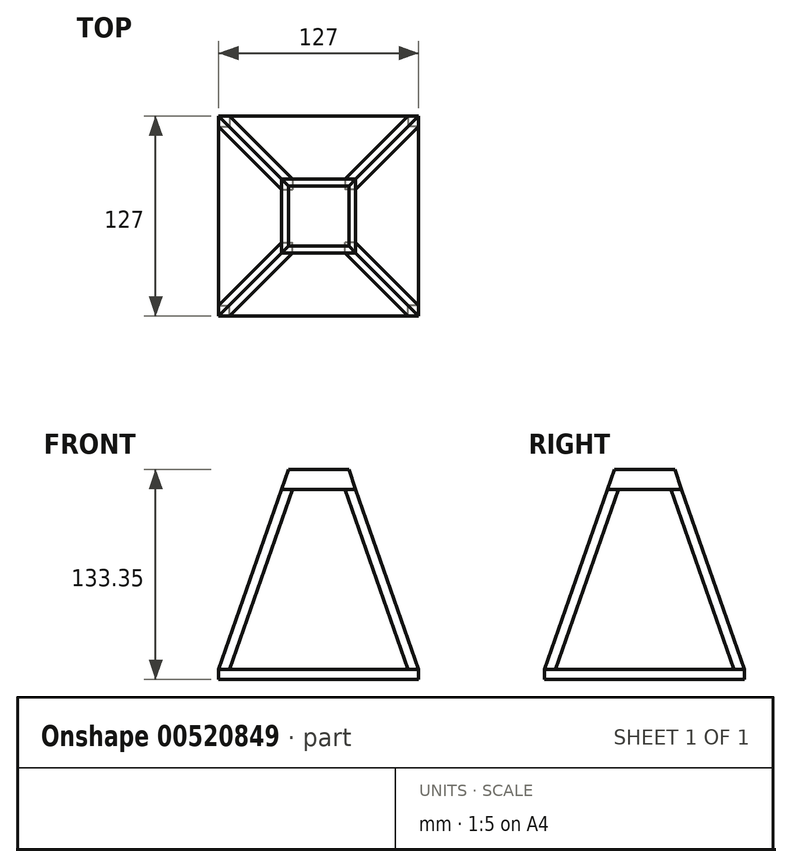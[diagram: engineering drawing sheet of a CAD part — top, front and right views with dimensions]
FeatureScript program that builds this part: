
annotation { "Feature Type Name" : "Feature", "Feature Type Description" : "" }
export const myFeature = defineFeature(function(context is Context, id is Id, definition is map)
    precondition{}
    {
        {
            var Q0;
            Q0=qCreatedBy(makeId("Top.planeOp"),FACE);
            var sketch = newSketch(context, id + "F0", { "sketchPlane" : qUnion([Q0])});
            skLineSegment(sketch, "E0.bottom", {"start": v(-63.5, 63.5) * mm, "end": v(63.5, 63.5) * mm});
            skLineSegment(sketch, "E0.top", {"start": v(-63.5, -63.5) * mm, "end": v(63.5, -63.5) * mm});
            skLineSegment(sketch, "E0.left", {"start": v(-63.5, 63.5) * mm, "end": v(-63.5, -63.5) * mm});
            skLineSegment(sketch, "E0.right", {"start": v(63.5, 63.5) * mm, "end": v(63.5, -63.5) * mm});
            skLineSegment(sketch, "E1", {"start": v(-63.5, 63.5) * mm, "end": v(63.5, -63.5) * mm, "construction": true});
            skLineSegment(sketch, "E2", {"start": v(-63.5, -63.5) * mm, "end": v(63.5, 63.5) * mm, "construction": true});
            skSolve(sketch);
        }
        {
            var Q0;
            Q0 = qSketchRegion(id + "F0", true);
            extrude(context, id + "F1", {"entities" : qUnion([Q0]), "depth" : 6.35 * mm, "offsetDistance" : 25.4 * mm});
        }
        {
            var Q0;
            Q0=makeQuery(id+"F1.opExtrude","CAP_FACE",FACE,{"disambiguationData":[OSD([sQuery(id+"F0.wireOp",EDGE,"E0.bottom"),sQuery(id+"F0.wireOp",EDGE,"E0.top"),sQuery(id+"F0.wireOp",EDGE,"E0.left"),sQuery(id+"F0.wireOp",EDGE,"E0.right")])],"isStart":false});
            cPlane(context, id + "F2", {"entities" : qUnion([Q0]), "cplaneType" : CPlaneType.OFFSET, "offset" : 114.3 * mm, "width" : 152.4 * mm, "height" : 152.4 * mm});
        }
        {
            var Q0;
            Q0=qCreatedBy(id+"F2.planeOp",FACE);
            var sketch = newSketch(context, id + "F3", { "sketchPlane" : qUnion([Q0])});
            skLineSegment(sketch, "E3.bottom", {"start": v(-23.5, 23.5) * mm, "end": v(23.5, 23.5) * mm});
            skLineSegment(sketch, "E3.top", {"start": v(-23.5, -23.5) * mm, "end": v(23.5, -23.5) * mm});
            skLineSegment(sketch, "E3.left", {"start": v(-23.5, 23.5) * mm, "end": v(-23.5, -23.5) * mm});
            skLineSegment(sketch, "E3.right", {"start": v(23.5, 23.5) * mm, "end": v(23.5, -23.5) * mm});
            skLineSegment(sketch, "E4", {"start": v(-23.5, -23.5) * mm, "end": v(23.5, 23.5) * mm, "construction": true});
            skLineSegment(sketch, "E5", {"start": v(-23.5, 23.5) * mm, "end": v(23.5, -23.5) * mm, "construction": true});
            skSolve(sketch);
        }
        {
            var Q0;
            Q0=makeQuery(id+"F3.imprint","IMPRINT",FACE,{"disambiguationData":[TD([[makeQuery(id+"F3.imprint","IMPRINT",EDGE,{"derivedFrom":sQuery(id+"F3.wireOp",EDGE,"E3.bottom")}),-1.0]])]});
            extrude(context, id + "F4", {"entities" : qUnion([Q0]), "depth" : 12.7 * mm, "offsetDistance" : 25.4 * mm});
        }
        {
            var Q0;
            Q0=makeQuery(id+"F4.opExtrude","CAP_VERTEX",VERTEX,{"disambiguationData":[OSD([sQuery(id+"F3.wireOp",EDGE,"E3.top"),sQuery(id+"F3.wireOp",EDGE,"E3.left")])],"isStart":false});
            var Q1;
            Q1=makeQuery(id+"F4.opExtrude","CAP_VERTEX",VERTEX,{"disambiguationData":[OSD([sQuery(id+"F3.wireOp",EDGE,"E3.bottom"),sQuery(id+"F3.wireOp",EDGE,"E3.right")])],"isStart":false});
            var Q2;
            Q2=makeQuery(id+"F1.opExtrude","CAP_VERTEX",VERTEX,{"disambiguationData":[OSD([sQuery(id+"F0.wireOp",EDGE,"E0.top"),sQuery(id+"F0.wireOp",EDGE,"E0.left")])],"isStart":false});
            cPlane(context, id + "F5", {"entities" : qUnion([Q0, Q1, Q2]), "cplaneType" : CPlaneType.THREE_POINT, "offset" : 25.4 * mm, "width" : 152.4 * mm, "height" : 152.4 * mm});
        }
        {
            var Q0;
            Q0=qCreatedBy(id+"F5.planeOp",FACE);
            var sketch = newSketch(context, id + "F6", { "sketchPlane" : qUnion([Q0])});
            skPoint(sketch, "E6.0", {"position": v(-89.8, 6.35) * mm});
            skPoint(sketch, "E7.0", {"position": v(-33.23, 120.65) * mm});
            skLineSegment(sketch, "E8", {"start": v(-89.8, 6.35) * mm, "end": v(-33.23, 120.65) * mm});
            skLineSegment(sketch, "E9", {"start": v(-89.8, 6.35) * mm, "end": v(-82.72, 6.35) * mm, "construction": true});
            skLineSegment(sketch, "E10", {"start": v(-82.72, 6.35) * mm, "end": v(-26.14, 120.65) * mm, "construction": true});
            skLineSegment(sketch, "E11", {"start": v(-33.23, 120.65) * mm, "end": v(-26.14, 120.65) * mm, "construction": true});
            skLineSegment(sketch, "E12", {"start": v(-82.72, 6.35) * mm, "end": v(-88.4, 9.17) * mm, "construction": true});
            skSolve(sketch);
        }
        {
            var Q0;
            Q0=makeQuery(id+"F1.opExtrude","CAP_FACE",FACE,{"disambiguationData":[OSD([sQuery(id+"F0.wireOp",EDGE,"E0.bottom"),sQuery(id+"F0.wireOp",EDGE,"E0.top"),sQuery(id+"F0.wireOp",EDGE,"E0.left"),sQuery(id+"F0.wireOp",EDGE,"E0.right")])],"isStart":false});
            var sketch = newSketch(context, id + "F7", { "sketchPlane" : qUnion([Q0])});
            skLineSegment(sketch, "E13.bottom", {"start": v(-63.5, -63.5) * mm, "end": v(-56.77, -63.5) * mm});
            skLineSegment(sketch, "E13.top", {"start": v(-63.5, -56.77) * mm, "end": v(-56.77, -56.77) * mm});
            skLineSegment(sketch, "E13.left", {"start": v(-63.5, -63.5) * mm, "end": v(-63.5, -56.77) * mm});
            skLineSegment(sketch, "E13.right", {"start": v(-56.77, -63.5) * mm, "end": v(-56.77, -56.77) * mm});
            skSolve(sketch);
        }
        {
            var Q0;
            Q0 = qSketchRegion(id + "F7", true);
            var Q1;
            Q1=sQuery(id+"F6.wireOp",EDGE,"E8");
            sweep(context, id + "F8", {"profiles" : qUnion([Q0]), "path" : qUnion([Q1])});
        }
        {
            var Q0;
            Q0=qCreatedBy(makeId("Front.planeOp"),FACE);
            var sketch = newSketch(context, id + "F9", { "sketchPlane" : qUnion([Q0])});
            skLineSegment(sketch, "E14", {"start": v(0, 0) * mm, "end": v(0, 508) * mm, "construction": true});
            skSolve(sketch);
        }
        {
            var Q0;
            Q0=makeQuery(id+"F8.opSweep","SWEPT_BODY",BODY,{"disambiguationData":[OSD([sQuery(id+"F6.wireOp",EDGE,"E8"),sQuery(id+"F7.wireOp",EDGE,"E13.bottom"),sQuery(id+"F7.wireOp",EDGE,"E13.top"),sQuery(id+"F7.wireOp",EDGE,"E13.left"),sQuery(id+"F7.wireOp",EDGE,"E13.right")])]});
            var Q1;
            Q1=sQuery(id+"F9.wireOp",EDGE,"E14");
            circularPattern(context, id + "F10", {"entities" : qUnion([Q0]), "axis" : qUnion([Q1]), "angle" : 360 * degree, "instanceCount" : 4, "equalSpace" : true});
        }
        {
            var Q0;
            Q0=makeQuery(id+"F8.opSweep","SWEPT_FACE",FACE,{"disambiguationData":[OSD([sQuery(id+"F6.wireOp",EDGE,"E8"),sQuery(id+"F7.wireOp",EDGE,"E13.bottom")])]});
            cPlane(context, id + "F11", {"entities" : qUnion([Q0]), "cplaneType" : CPlaneType.OFFSET, "offset" : 0 * mm, "width" : 152.4 * mm, "height" : 152.4 * mm});
        }
        {
            var Q0;
            Q0=makeQuery(id+"F4.opExtrude","CAP_EDGE",EDGE,{"disambiguationData":[OSD([sQuery(id+"F3.wireOp",EDGE,"E3.left")])],"isStart":false});
            var Q1;
            Q1=makeQuery(id+"F4.opExtrude","CAP_EDGE",EDGE,{"disambiguationData":[OSD([sQuery(id+"F3.wireOp",EDGE,"E3.top")])],"isStart":false});
            var Q2;
            Q2=makeQuery(id+"F4.opExtrude","CAP_EDGE",EDGE,{"disambiguationData":[OSD([sQuery(id+"F3.wireOp",EDGE,"E3.bottom")])],"isStart":false});
            var Q3;
            Q3=makeQuery(id+"F4.opExtrude","CAP_EDGE",EDGE,{"disambiguationData":[OSD([sQuery(id+"F3.wireOp",EDGE,"E3.right")])],"isStart":false});
            chamfer(context, id + "F12", {"entities" : qUnion([Q0, Q1, Q2, Q3]), "chamferType" : ChamferType.OFFSET_ANGLE, "width" : 4.37 * mm, "oppositeDirection" : false, "angle" : 71 * degree, "tangentPropagation" : true});
        }
    });
